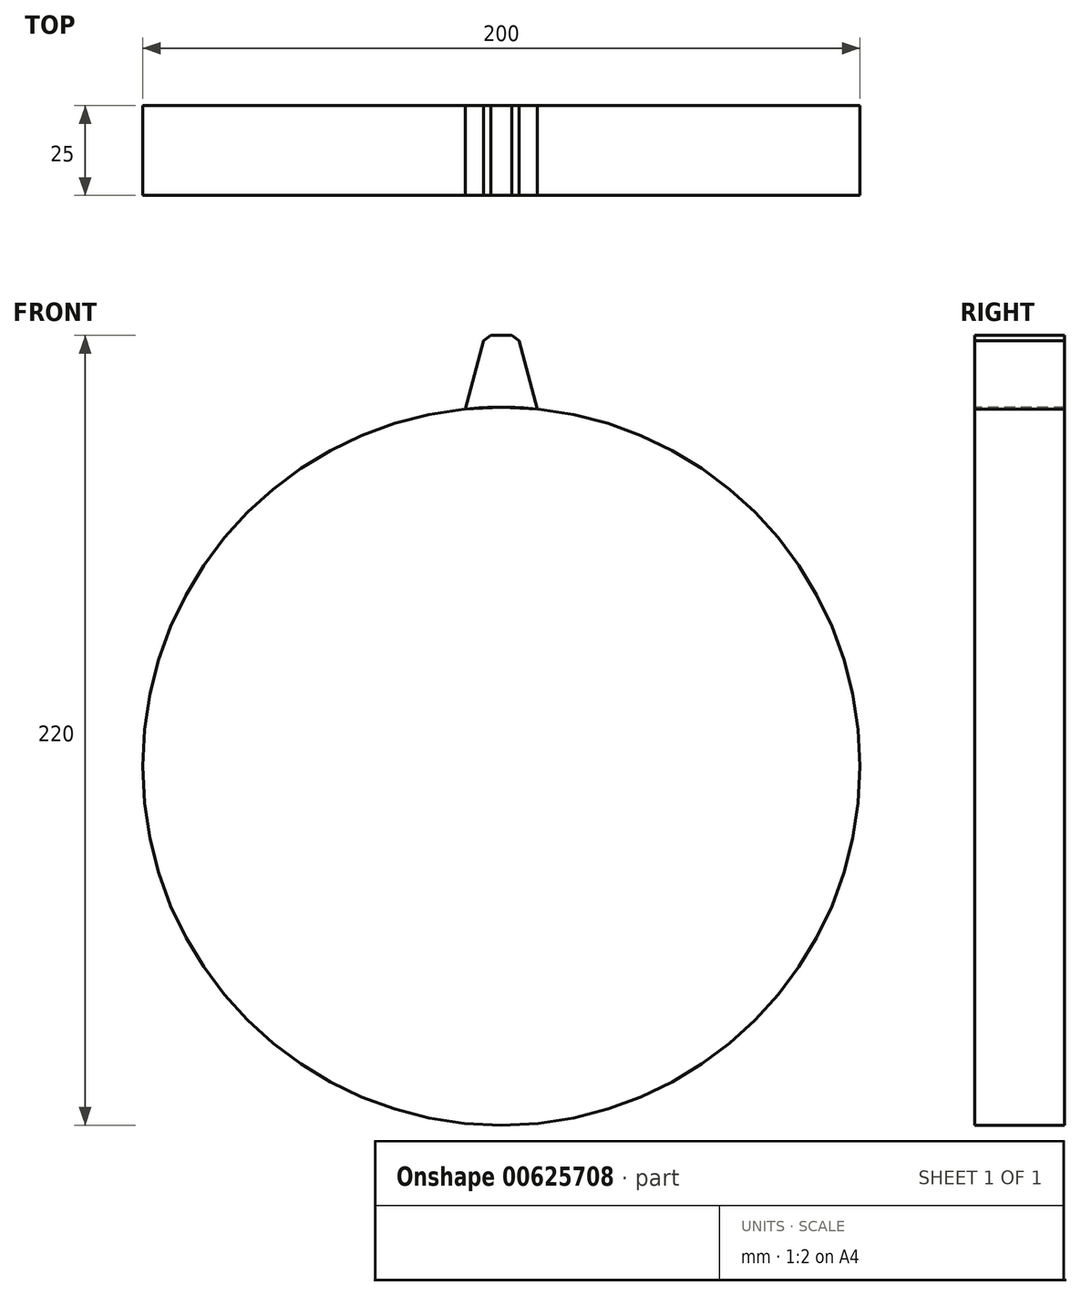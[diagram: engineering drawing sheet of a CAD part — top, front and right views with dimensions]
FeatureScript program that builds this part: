
annotation { "Feature Type Name" : "Feature", "Feature Type Description" : "" }
export const myFeature = defineFeature(function(context is Context, id is Id, definition is map)
    precondition{}
    {
        {
            var Q0;
            Q0=qCreatedBy(makeId("Front.planeOp"),FACE);
            var sketch = newSketch(context, id + "F0", { "sketchPlane" : qUnion([Q0])});
            skCircle(sketch, "E0", {"center": v(0, 0) * mm, "radius": 100 * mm});
            skSolve(sketch);
        }
        {
            var Q0;
            Q0=makeQuery(id+"F0.imprint","IMPRINT",FACE,{"disambiguationData":[TD([[makeQuery(id+"F0.imprint","IMPRINT",EDGE,{"derivedFrom":sQuery(id+"F0.wireOp",EDGE,"E0")}),1.0]])]});
            extrude(context, id + "F1", {"entities" : qUnion([Q0]), "depth" : 25 * mm, "offsetDistance" : 25 * mm});
        }
        {
            var Q0;
            Q0=makeQuery(id+"F1.opExtrude","CAP_FACE",FACE,{"disambiguationData":[OSD([sQuery(id+"F0.wireOp",EDGE,"E0")])],"isStart":false});
            var sketch = newSketch(context, id + "F2", { "sketchPlane" : qUnion([Q0])});
            skLineSegment(sketch, "E1", {"start": v(-4.5, 120) * mm, "end": v(4.5, 120) * mm});
            skLineSegment(sketch, "E2", {"start": v(4.5, 120) * mm, "end": v(10, 99.5) * mm});
            skLineSegment(sketch, "E3", {"start": v(10, 99.5) * mm, "end": v(-10, 99.5) * mm});
            skLineSegment(sketch, "E4", {"start": v(-10, 99.5) * mm, "end": v(-4.5, 120) * mm});
            skSolve(sketch);
        }
        {
            var Q0;
            Q0=makeQuery(id+"F2.imprint","IMPRINT",FACE,{"disambiguationData":[TD([[makeQuery(id+"F2.imprint","IMPRINT",EDGE,{"derivedFrom":sQuery(id+"F2.wireOp",EDGE,"E1")}),-1.0]])]});
            extrude(context, id + "F3", {"entities" : qUnion([Q0]), "oppositeDirection" : true, "depth" : 25 * mm, "offsetDistance" : 25 * mm});
        }
        {
            var Q0;
            Q0=makeQuery(id+"F3.opExtrude","SWEPT_EDGE",EDGE,{"disambiguationData":[OSD([sQuery(id+"F2.wireOp",EDGE,"E1"),sQuery(id+"F2.wireOp",EDGE,"E2")])]});
            var Q1;
            Q1=makeQuery(id+"F3.opExtrude","SWEPT_EDGE",EDGE,{"disambiguationData":[OSD([sQuery(id+"F2.wireOp",EDGE,"E1"),sQuery(id+"F2.wireOp",EDGE,"E4")])]});
            chamfer(context, id + "F4", {"entities" : qUnion([Q0, Q1]), "width" : 2 * mm, "tangentPropagation" : true});
        }
    });
